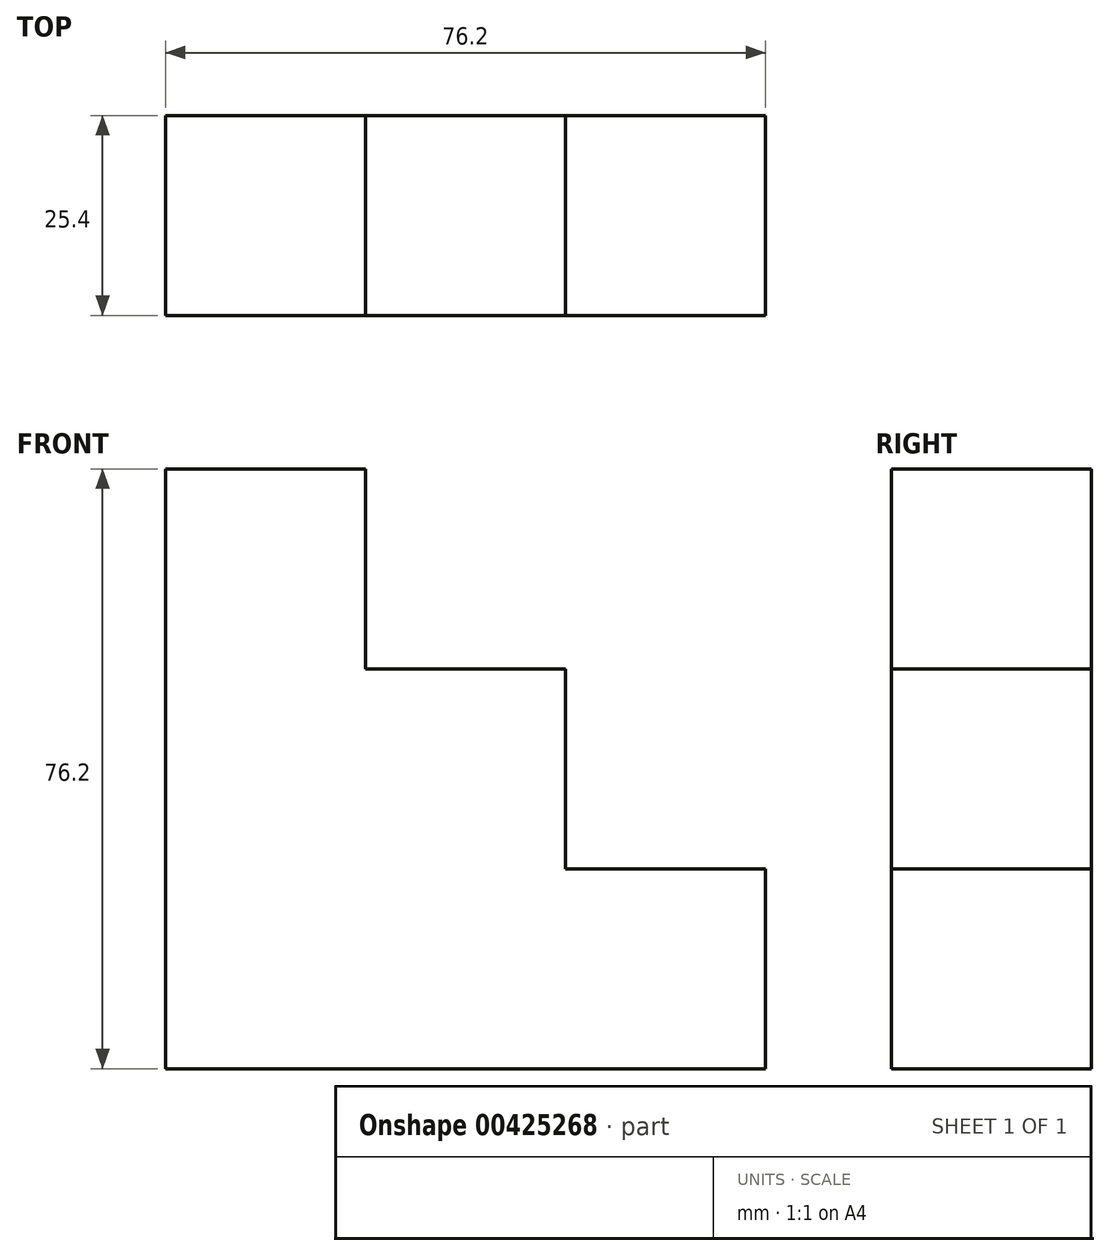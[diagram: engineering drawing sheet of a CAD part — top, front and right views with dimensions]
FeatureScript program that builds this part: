
annotation { "Feature Type Name" : "Feature", "Feature Type Description" : "" }
export const myFeature = defineFeature(function(context is Context, id is Id, definition is map)
    precondition{}
    {
        {
            var Q0;
            Q0=qCreatedBy(makeId("Front.planeOp"),FACE);
            var sketch = newSketch(context, id + "F0", { "sketchPlane" : qUnion([Q0])});
            skLineSegment(sketch, "E0", {"start": v(-39.53, 87.28) * mm, "end": v(-39.53, 11.08) * mm});
            skLineSegment(sketch, "E1", {"start": v(-39.53, 11.08) * mm, "end": v(36.67, 11.08) * mm});
            skLineSegment(sketch, "E2", {"start": v(-39.53, 87.28) * mm, "end": v(-14.13, 87.28) * mm});
            skLineSegment(sketch, "E3", {"start": v(-14.13, 87.28) * mm, "end": v(-14.13, 61.88) * mm});
            skLineSegment(sketch, "E4", {"start": v(-14.13, 61.88) * mm, "end": v(11.27, 61.88) * mm});
            skLineSegment(sketch, "E5", {"start": v(11.27, 61.88) * mm, "end": v(11.27, 36.48) * mm});
            skLineSegment(sketch, "E6", {"start": v(11.27, 36.48) * mm, "end": v(36.67, 36.48) * mm});
            skLineSegment(sketch, "E7", {"start": v(36.67, 36.48) * mm, "end": v(36.67, 11.08) * mm});
            skSolve(sketch);
        }
        {
            var Q0;
            Q0=makeQuery(id+"F0.imprint","IMPRINT",FACE,{"disambiguationData":[TD([[makeQuery(id+"F0.imprint","IMPRINT",EDGE,{"derivedFrom":sQuery(id+"F0.wireOp",EDGE,"E0")}),1.0]])]});
            extrude(context, id + "F1", {"entities" : qUnion([Q0]), "depth" : 25.4 * mm});
        }
    });
